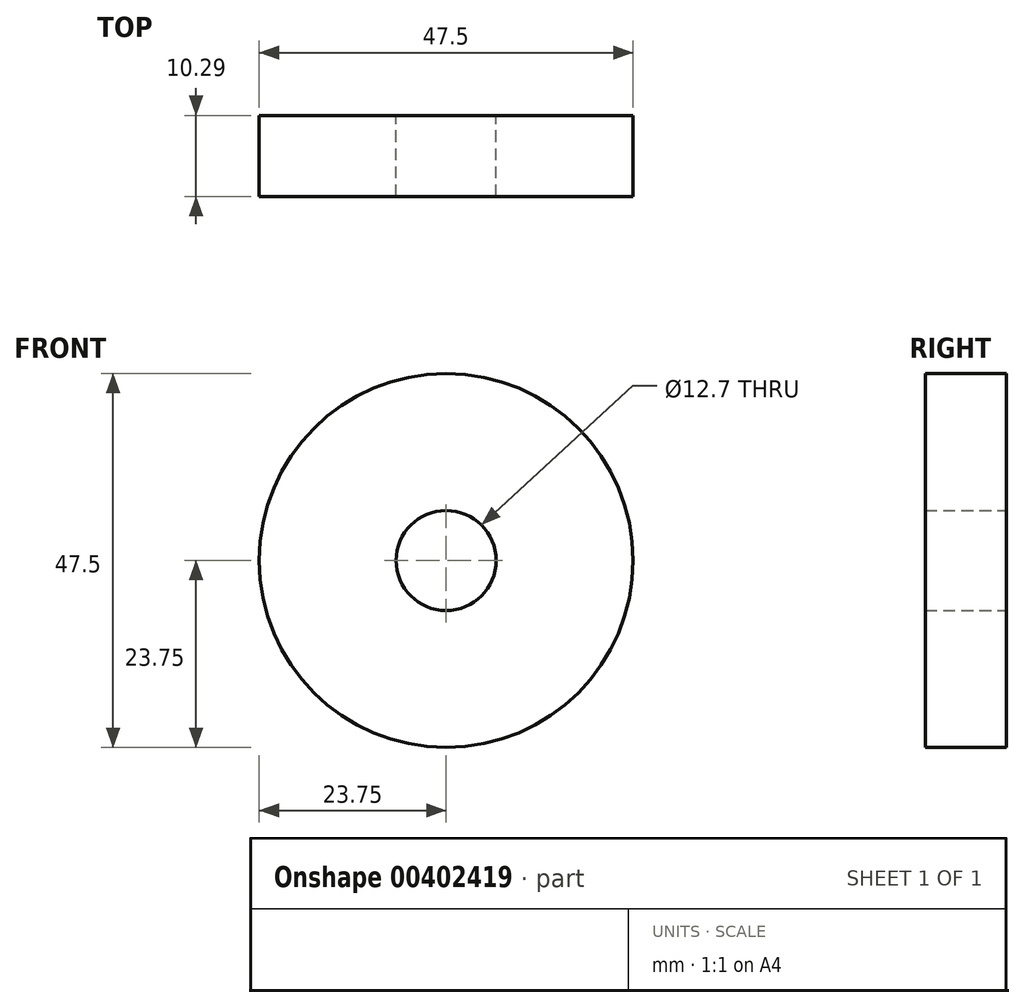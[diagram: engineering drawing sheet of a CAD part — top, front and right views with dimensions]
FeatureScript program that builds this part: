
annotation { "Feature Type Name" : "Feature", "Feature Type Description" : "" }
export const myFeature = defineFeature(function(context is Context, id is Id, definition is map)
    precondition{}
    {
        {
            var Q0;
            Q0=qCreatedBy(makeId("Front.planeOp"),FACE);
            var sketch = newSketch(context, id + "F0", { "sketchPlane" : qUnion([Q0])});
            skCircle(sketch, "E0", {"center": v(0, 0) * mm, "radius": 23.75 * mm});
            skCircle(sketch, "E1", {"center": v(0, 0) * mm, "radius": 6.35 * mm});
            skSolve(sketch);
        }
        {
            var Q0;
            Q0=makeQuery(id+"F0.imprint","IMPRINT",FACE,{"disambiguationData":[TD([[makeQuery(id+"F0.imprint","IMPRINT",EDGE,{"derivedFrom":sQuery(id+"F0.wireOp",EDGE,"E0")}),1.0]])]});
            extrude(context, id + "F1", {"entities" : qUnion([Q0]), "depth" : 10.29 * mm});
        }
    });
